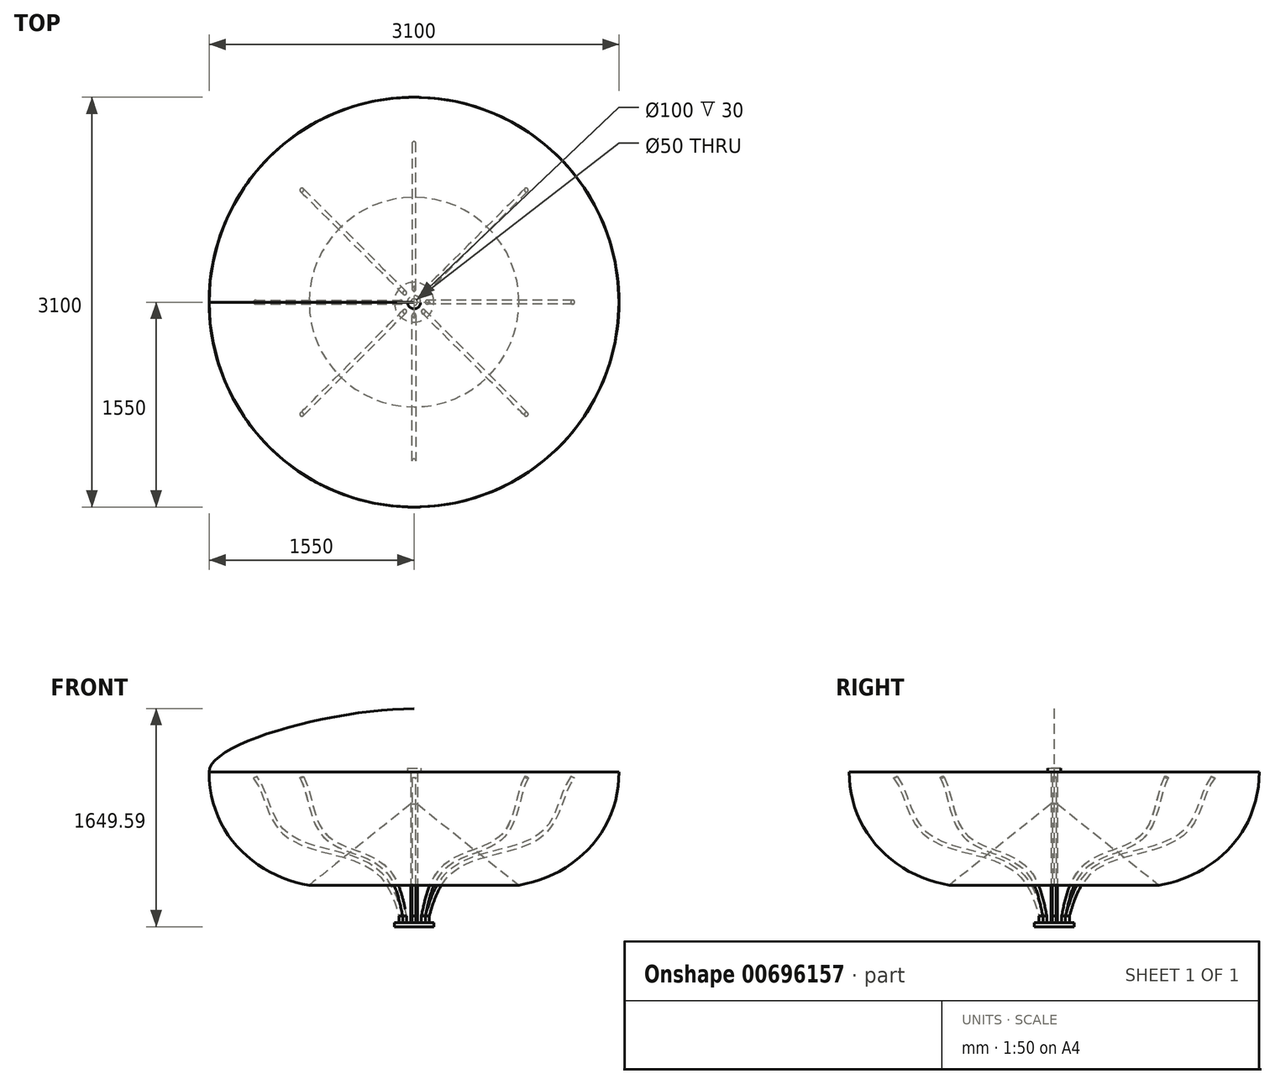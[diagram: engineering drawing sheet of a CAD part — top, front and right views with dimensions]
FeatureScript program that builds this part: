
annotation { "Feature Type Name" : "Feature", "Feature Type Description" : "" }
export const myFeature = defineFeature(function(context is Context, id is Id, definition is map)
    precondition{}
    {
        {
            var Q0;
            Q0=qCreatedBy(makeId("Top.planeOp"),FACE);
            var sketch = newSketch(context, id + "F0", { "sketchPlane" : qUnion([Q0])});
            skCircle(sketch, "E0", {"center": v(0, 0) * mm, "radius": 150 * mm});
            skSolve(sketch);
        }
        {
            var Q0;
            Q0 = qSketchRegion(id + "F0", true);
            extrude(context, id + "F1", {"entities" : qUnion([Q0]), "depth" : 30 * mm, "offsetDistance" : 25 * mm});
        }
        {
            var Q0;
            Q0=makeQuery(id+"F1.opExtrude","CAP_FACE",FACE,{"disambiguationData":[OSD([sQuery(id+"F0.wireOp",EDGE,"E0")])],"isStart":false});
            var sketch = newSketch(context, id + "F2", { "sketchPlane" : qUnion([Q0])});
            skCircle(sketch, "E1", {"center": v(0, 0) * mm, "radius": 25 * mm});
            skSolve(sketch);
        }
        {
            var Q0;
            Q0 = qSketchRegion(id + "F2", true);
            extrude(context, id + "F3", {"entities" : qUnion([Q0]), "operationType" : NewBodyOperationType.ADD, "depth" : 1140 * mm, "offsetDistance" : 25 * mm});
        }
        {
            var Q0;
            Q0=makeQuery(id+"F3.opExtrude","CAP_FACE",FACE,{"disambiguationData":[OSD([sQuery(id+"F2.wireOp",EDGE,"E1")])],"isStart":false});
            var sketch = newSketch(context, id + "F4", { "sketchPlane" : qUnion([Q0])});
            skCircle(sketch, "E2", {"center": v(0, 0) * mm, "radius": 50 * mm});
            skSolve(sketch);
        }
        {
            var Q0;
            Q0 = qSketchRegion(id + "F4", true);
            extrude(context, id + "F5", {"entities" : qUnion([Q0]), "operationType" : NewBodyOperationType.ADD, "depth" : 30 * mm, "offsetDistance" : 25 * mm});
        }
        {
            var Q0;
            Q0=makeQuery(id+"F1.opExtrude","CAP_FACE",FACE,{"disambiguationData":[OSD([sQuery(id+"F0.wireOp",EDGE,"E0")])],"isStart":false});
            var sketch = newSketch(context, id + "F6", { "sketchPlane" : qUnion([Q0])});
            skCircle(sketch, "E3", {"center": v(0, 100) * mm, "radius": 15 * mm});
            skCircle(sketch, "E4.1.0", {"center": v(70.71, 70.71) * mm, "radius": 15 * mm});
            skCircle(sketch, "E4.2.0", {"center": v(100, 0) * mm, "radius": 15 * mm});
            skCircle(sketch, "E4.3.0", {"center": v(70.71, -70.71) * mm, "radius": 15 * mm});
            skCircle(sketch, "E4.4.0", {"center": v(0, -100) * mm, "radius": 15 * mm});
            skCircle(sketch, "E4.5.0", {"center": v(-70.71, -70.71) * mm, "radius": 15 * mm});
            skCircle(sketch, "E4.6.0", {"center": v(-100, 0) * mm, "radius": 15 * mm});
            skCircle(sketch, "E4.7.0", {"center": v(-70.71, 70.71) * mm, "radius": 15 * mm});
            skPoint(sketch, "E4.center", {"position": v(0, 0) * mm});
            skLineSegment(sketch, "E4.anchor1", {"start": v(0, 0) * mm, "end": v(0, 100) * mm, "construction": true});
            skLineSegment(sketch, "E4.anchor2", {"start": v(0, 0) * mm, "end": v(-70.71, 70.71) * mm, "construction": true});
            skSolve(sketch);
        }
        {
            var Q0;
            Q0 = qSketchRegion(id + "F6", true);
            extrude(context, id + "F7", {"entities" : qUnion([Q0]), "operationType" : NewBodyOperationType.ADD, "depth" : 50 * mm, "offsetDistance" : 25 * mm});
        }
        {
            var Q0;
            Q0=makeQuery(id+"F1.opExtrude","CAP_FACE",FACE,{"disambiguationData":[OSD([sQuery(id+"F0.wireOp",EDGE,"E0")])],"isStart":false});
            var sketch = newSketch(context, id + "F8", { "sketchPlane" : qUnion([Q0])});
            skLineSegment(sketch, "E5", {"start": v(-70.71, -70.71) * mm, "end": v(70.71, 70.71) * mm, "construction": true});
            skLineSegment(sketch, "E6", {"start": v(-100, 0) * mm, "end": v(100, 0) * mm, "construction": true});
            skLineSegment(sketch, "E7", {"start": v(-70.71, 70.71) * mm, "end": v(70.71, -70.71) * mm, "construction": true});
            skLineSegment(sketch, "E8", {"start": v(0, 100) * mm, "end": v(0, -100) * mm, "construction": true});
            skSolve(sketch);
        }
        {
            var Q0;
            Q0=sQuery(id+"F8.wireOp",EDGE,"E5");
            var Q1;
            Q1=qCreatedBy(makeId("Origin.pointOp"),VERTEX);
            cPlane(context, id + "F9", {"entities" : qUnion([Q0, Q1]), "cplaneType" : CPlaneType.LINE_POINT, "offset" : 25 * mm, "width" : 150 * mm, "height" : 150 * mm});
        }
        {
            var Q0;
            Q0=sQuery(id+"F8.wireOp",EDGE,"E6");
            var Q1;
            Q1=qCreatedBy(makeId("Origin.pointOp"),VERTEX);
            cPlane(context, id + "F10", {"entities" : qUnion([Q0, Q1]), "cplaneType" : CPlaneType.LINE_POINT, "offset" : 25 * mm, "width" : 150 * mm, "height" : 150 * mm});
        }
        {
            var Q0;
            Q0=sQuery(id+"F8.wireOp",EDGE,"E7");
            var Q1;
            Q1=qCreatedBy(makeId("Origin.pointOp"),VERTEX);
            cPlane(context, id + "F11", {"entities" : qUnion([Q0, Q1]), "cplaneType" : CPlaneType.LINE_POINT, "offset" : 25 * mm, "width" : 150 * mm, "height" : 150 * mm});
        }
        {
            var Q0;
            Q0=sQuery(id+"F8.wireOp",EDGE,"E8");
            var Q1;
            Q1=qCreatedBy(makeId("Origin.pointOp"),VERTEX);
            cPlane(context, id + "F12", {"entities" : qUnion([Q0, Q1]), "cplaneType" : CPlaneType.LINE_POINT, "offset" : 25 * mm, "width" : 150 * mm, "height" : 150 * mm});
        }
        {
            var Q0;
            Q0=makeQuery(id+"F7.opExtrude","CAP_FACE",FACE,{"disambiguationData":[OSD([sQuery(id+"F6.wireOp",EDGE,"E4.6.0")])],"isStart":false});
            var sketch = newSketch(context, id + "F13", { "sketchPlane" : qUnion([Q0])});
            skCircle(sketch, "E9", {"center": v(-100, 0) * mm, "radius": 15 * mm});
            skCircle(sketch, "E10.1.0", {"center": v(-70.71, -70.71) * mm, "radius": 15 * mm});
            skCircle(sketch, "E10.2.0", {"center": v(0, -100) * mm, "radius": 15 * mm});
            skCircle(sketch, "E10.3.0", {"center": v(70.71, -70.71) * mm, "radius": 15 * mm});
            skCircle(sketch, "E10.4.0", {"center": v(100, 0) * mm, "radius": 15 * mm});
            skCircle(sketch, "E10.5.0", {"center": v(70.71, 70.71) * mm, "radius": 15 * mm});
            skCircle(sketch, "E10.6.0", {"center": v(0, 100) * mm, "radius": 15 * mm});
            skCircle(sketch, "E10.7.0", {"center": v(-70.71, 70.71) * mm, "radius": 15 * mm});
            skPoint(sketch, "E10.center", {"position": v(0, 0) * mm});
            skSolve(sketch);
        }
        {
            var Q0;
            Q0=qCreatedBy(id+"F12.planeOp",FACE);
            var sketch = newSketch(context, id + "F14", { "sketchPlane" : qUnion([Q0])});
            skFitSpline(sketch, "E11", {"points": [v(-100, 80) * mm, v(-200, 330) * mm, v(-500, 530) * mm, v(-1000, 730) * mm, v(-1200, 1130) * mm], "startDerivative": vector(-206.81, 684.14) * mm, "endDerivative": vector(-873.41, 1074.38) * mm});
            skLineSegment(sketch, "E12", {"start": v(0, 0) * mm, "end": v(0, 1445.65) * mm, "construction": true});
            skFitSpline(sketch, "E13.MirrorCS", {"points": [v(100, 80) * mm, v(200, 330) * mm, v(500, 530) * mm, v(1000, 730) * mm, v(1200, 1130) * mm], "startDerivative": vector(206.81, 684.14) * mm, "endDerivative": vector(873.41, 1074.38) * mm});
            skSolve(sketch);
        }
        {
            var Q0;
            Q0=makeQuery(id+"F13.imprint","IMPRINT",FACE,{"disambiguationData":[TD([[makeQuery(id+"F13.imprint","IMPRINT",EDGE,{"derivedFrom":sQuery(id+"F13.wireOp",EDGE,"E9")}),1.0]])]});
            var Q1;
            Q1=sQuery(id+"F14.wireOp",EDGE,"E11");
            sweep(context, id + "F15", {"operationType" : NewBodyOperationType.ADD, "profiles" : qUnion([Q0]), "path" : qUnion([Q1])});
        }
        {
            var Q0;
            Q0=makeQuery(id+"F13.imprint","IMPRINT",FACE,{"disambiguationData":[TD([[makeQuery(id+"F13.imprint","IMPRINT",EDGE,{"derivedFrom":sQuery(id+"F13.wireOp",EDGE,"E10.4.0")}),1.0]])]});
            var Q1;
            Q1=sQuery(id+"F13.wireOp",EDGE,"E10.4.0");
            var Q2;
            Q2=sQuery(id+"F14.wireOp",EDGE,"E13.MirrorCS");
            sweep(context, id + "F16", {"operationType" : NewBodyOperationType.ADD, "profiles" : qUnion([Q0]), "surfaceOperationType" : NewSurfaceOperationType.ADD, "surfaceProfiles" : qUnion([Q1]), "path" : qUnion([Q2])});
        }
        {
            var Q0;
            Q0=qCreatedBy(id+"F9.planeOp",FACE);
            var sketch = newSketch(context, id + "F17", { "sketchPlane" : qUnion([Q0])});
            skFitSpline(sketch, "E14", {"points": [v(-100, 80) * mm, v(-200, 330) * mm, v(-500, 530) * mm, v(-1000, 730) * mm, v(-1200, 1130) * mm], "startDerivative": vector(-206.81, 684.14) * mm, "endDerivative": vector(-873.41, 1074.38) * mm});
            skLineSegment(sketch, "E15", {"start": v(0, 0) * mm, "end": v(0, 1445.65) * mm, "construction": true});
            skFitSpline(sketch, "E16.MirrorCS", {"points": [v(100, 80) * mm, v(200, 330) * mm, v(500, 530) * mm, v(1000, 730) * mm, v(1200, 1130) * mm], "startDerivative": vector(206.81, 684.14) * mm, "endDerivative": vector(873.41, 1074.38) * mm});
            skSolve(sketch);
        }
        {
            var Q0;
            Q0=makeQuery(id+"F13.imprint","IMPRINT",FACE,{"disambiguationData":[TD([[makeQuery(id+"F13.imprint","IMPRINT",EDGE,{"derivedFrom":sQuery(id+"F13.wireOp",EDGE,"E10.7.0")}),1.0]])]});
            var Q1;
            Q1=sQuery(id+"F13.wireOp",EDGE,"E10.7.0");
            var Q2;
            Q2=sQuery(id+"F17.wireOp",EDGE,"E16.MirrorCS");
            var Q3;
            Q3=sQuery(id+"F17.wireOp",EDGE,"E16.MirrorCS");
            sweep(context, id + "F18", {"operationType" : NewBodyOperationType.ADD, "profiles" : qUnion([Q0]), "surfaceProfiles" : qUnion([Q1, Q2]), "path" : qUnion([Q3])});
        }
        {
            var Q0;
            Q0=makeQuery(id+"F13.imprint","IMPRINT",FACE,{"disambiguationData":[TD([[makeQuery(id+"F13.imprint","IMPRINT",EDGE,{"derivedFrom":sQuery(id+"F13.wireOp",EDGE,"E10.3.0")}),1.0]])]});
            var Q1;
            Q1=sQuery(id+"F13.wireOp",EDGE,"E10.3.0");
            var Q2;
            Q2=sQuery(id+"F17.wireOp",EDGE,"E14");
            sweep(context, id + "F19", {"operationType" : NewBodyOperationType.ADD, "profiles" : qUnion([Q0]), "surfaceProfiles" : qUnion([Q1]), "path" : qUnion([Q2])});
        }
        {
            var Q0;
            Q0=qCreatedBy(id+"F10.planeOp",FACE);
            var sketch = newSketch(context, id + "F20", { "sketchPlane" : qUnion([Q0])});
            skFitSpline(sketch, "E17", {"points": [v(-100, 80) * mm, v(-200, 330) * mm, v(-500, 530) * mm, v(-1000, 730) * mm, v(-1200, 1130) * mm], "startDerivative": vector(-206.81, 684.14) * mm, "endDerivative": vector(-873.41, 1074.38) * mm});
            skLineSegment(sketch, "E18", {"start": v(0, 0) * mm, "end": v(0, 1445.65) * mm, "construction": true});
            skFitSpline(sketch, "E19.MirrorCS", {"points": [v(100, 80) * mm, v(200, 330) * mm, v(500, 530) * mm, v(1000, 730) * mm, v(1200, 1130) * mm], "startDerivative": vector(206.81, 684.14) * mm, "endDerivative": vector(873.41, 1074.38) * mm});
            skSolve(sketch);
        }
        {
            var Q0;
            Q0=makeQuery(id+"F13.imprint","IMPRINT",FACE,{"disambiguationData":[TD([[makeQuery(id+"F13.imprint","IMPRINT",EDGE,{"derivedFrom":sQuery(id+"F13.wireOp",EDGE,"E10.6.0")}),1.0]])]});
            var Q1;
            Q1=sQuery(id+"F13.wireOp",EDGE,"E10.6.0");
            var Q2;
            Q2=sQuery(id+"F20.wireOp",EDGE,"E19.MirrorCS");
            sweep(context, id + "F21", {"operationType" : NewBodyOperationType.ADD, "profiles" : qUnion([Q0]), "surfaceOperationType" : NewSurfaceOperationType.ADD, "surfaceProfiles" : qUnion([Q1]), "path" : qUnion([Q2])});
        }
        {
            var Q0;
            Q0=makeQuery(id+"F13.imprint","IMPRINT",FACE,{"disambiguationData":[TD([[makeQuery(id+"F13.imprint","IMPRINT",EDGE,{"derivedFrom":sQuery(id+"F13.wireOp",EDGE,"E10.2.0")}),1.0]])]});
            var Q1;
            Q1=sQuery(id+"F20.wireOp",EDGE,"E17");
            sweep(context, id + "F22", {"operationType" : NewBodyOperationType.ADD, "profiles" : qUnion([Q0]), "path" : qUnion([Q1])});
        }
        {
            var Q0;
            Q0=qCreatedBy(id+"F11.planeOp",FACE);
            var sketch = newSketch(context, id + "F23", { "sketchPlane" : qUnion([Q0])});
            skFitSpline(sketch, "E20", {"points": [v(-100, 80) * mm, v(-200, 330) * mm, v(-500, 530) * mm, v(-1000, 730) * mm, v(-1200, 1130) * mm], "startDerivative": vector(-206.81, 684.14) * mm, "endDerivative": vector(-873.41, 1074.38) * mm});
            skLineSegment(sketch, "E21", {"start": v(0, 0) * mm, "end": v(0, 1445.65) * mm, "construction": true});
            skFitSpline(sketch, "E22.MirrorCS", {"points": [v(100, 80) * mm, v(200, 330) * mm, v(500, 530) * mm, v(1000, 730) * mm, v(1200, 1130) * mm], "startDerivative": vector(206.81, 684.14) * mm, "endDerivative": vector(873.41, 1074.38) * mm});
            skSolve(sketch);
        }
        {
            var Q0;
            Q0=makeQuery(id+"F13.imprint","IMPRINT",FACE,{"disambiguationData":[TD([[makeQuery(id+"F13.imprint","IMPRINT",EDGE,{"derivedFrom":sQuery(id+"F13.wireOp",EDGE,"E10.5.0")}),1.0]])]});
            var Q1;
            Q1=sQuery(id+"F23.wireOp",EDGE,"E22.MirrorCS");
            sweep(context, id + "F24", {"operationType" : NewBodyOperationType.ADD, "profiles" : qUnion([Q0]), "path" : qUnion([Q1])});
        }
        {
            var Q0;
            Q0=makeQuery(id+"F13.imprint","IMPRINT",FACE,{"disambiguationData":[TD([[makeQuery(id+"F13.imprint","IMPRINT",EDGE,{"derivedFrom":sQuery(id+"F13.wireOp",EDGE,"E10.1.0")}),1.0]])]});
            var Q1;
            Q1=sQuery(id+"F23.wireOp",EDGE,"E20");
            sweep(context, id + "F25", {"operationType" : NewBodyOperationType.ADD, "profiles" : qUnion([Q0]), "path" : qUnion([Q1])});
        }
        {
            var Q0;
            Q0=qCreatedBy(makeId("Front.planeOp"),FACE);
            var sketch = newSketch(context, id + "F26", { "sketchPlane" : qUnion([Q0])});
            skLineSegment(sketch, "E23", {"start": v(-50, 1170) * mm, "end": v(-50, 1200) * mm});
            skLineSegment(sketch, "E24", {"start": v(50, 1200) * mm, "end": v(50, 1170) * mm});
            skLineSegment(sketch, "E25", {"start": v(-25, 30) * mm, "end": v(-25, 1170) * mm});
            skLineSegment(sketch, "E26", {"start": v(25, 1170) * mm, "end": v(25, 30) * mm});
            skLineSegment(sketch, "E27", {"start": v(0, 1200) * mm, "end": v(0, 1649.6) * mm});
            skLineSegment(sketch, "E28", {"start": v(-50, 1170) * mm, "end": v(-1550, 1170) * mm});
            skFitSpline(sketch, "E29", {"points": [v(0, 1649.6) * mm, v(-1550, 1170) * mm], "startDerivative": vector(-1750.59, 0) * mm, "endDerivative": vector(0, -681.4) * mm});
            skLineSegment(sketch, "E30", {"start": v(0, 1200) * mm, "end": v(-50, 1200) * mm});
            skSolve(sketch);
        }
        {
            var Q0;
            Q0 = qSketchRegion(id + "F26", true);
            var Q1;
            Q1=sQuery(id+"F26.wireOp",EDGE,"E27");
            revolve(context, id + "F27", {"surfaceOperationType" : NewSurfaceOperationType.NEW, "entities" : qUnion([Q0]), "axis" : qUnion([Q1]), "revolveType" : RevolveType.FULL});
        }
        {
            var Q0;
            Q0=qCreatedBy(makeId("Front.planeOp"),FACE);
            var sketch = newSketch(context, id + "F28", { "sketchPlane" : qUnion([Q0])});
            skLineSegment(sketch, "E31.0.0", {"start": v(50, 1170) * mm, "end": v(-50, 1170) * mm});
            skLineSegment(sketch, "E32", {"start": v(-50, 1170) * mm, "end": v(-1550, 1170) * mm});
            skLineSegment(sketch, "E33", {"start": v(-25, 30) * mm, "end": v(-25, 1170) * mm});
            skLineSegment(sketch, "E34", {"start": v(25, 1170) * mm, "end": v(25, 30) * mm});
            skLineSegment(sketch, "E35", {"start": v(-50, 1170) * mm, "end": v(-25, 1170) * mm});
            skLineSegment(sketch, "E36", {"start": v(-25, 927.89) * mm, "end": v(-793.3, 313.9) * mm});
            skFitSpline(sketch, "E37", {"points": [v(-1550, 1170) * mm, v(-793.3, 313.9) * mm], "startDerivative": vector(0, -1415.7) * mm, "endDerivative": vector(1193.93, -197.04) * mm});
            skLineSegment(sketch, "E38", {"start": v(0, 0) * mm, "end": v(0, 1406.69) * mm, "construction": true});
            skSolve(sketch);
        }
        {
            var Q0;
            {var subQ4=sQuery(id+"F28.wireOp",EDGE,"E32");Q0=makeQuery(id+"F28.imprint","IMPRINT",FACE,{"disambiguationData":[TD([[makeQuery(id+"F28.imprint","IMPRINT",EDGE,{"derivedFrom":subQ4}),1.0]])]});}
            var Q1;
            Q1=sQuery(id+"F28.wireOp",EDGE,"E37");
            var Q2;
            Q2=sQuery(id+"F28.wireOp",EDGE,"E36");
            var Q3;
            Q3=sQuery(id+"F28.wireOp",EDGE,"E32");
            var Q4;
            Q4=sQuery(id+"F28.wireOp",EDGE,"E38");
            revolve(context, id + "F29", {"surfaceOperationType" : NewSurfaceOperationType.NEW, "entities" : qUnion([Q0]), "surfaceEntities" : qUnion([Q1, Q2, Q3]), "axis" : qUnion([Q4]), "revolveType" : RevolveType.FULL});
        }
    });
